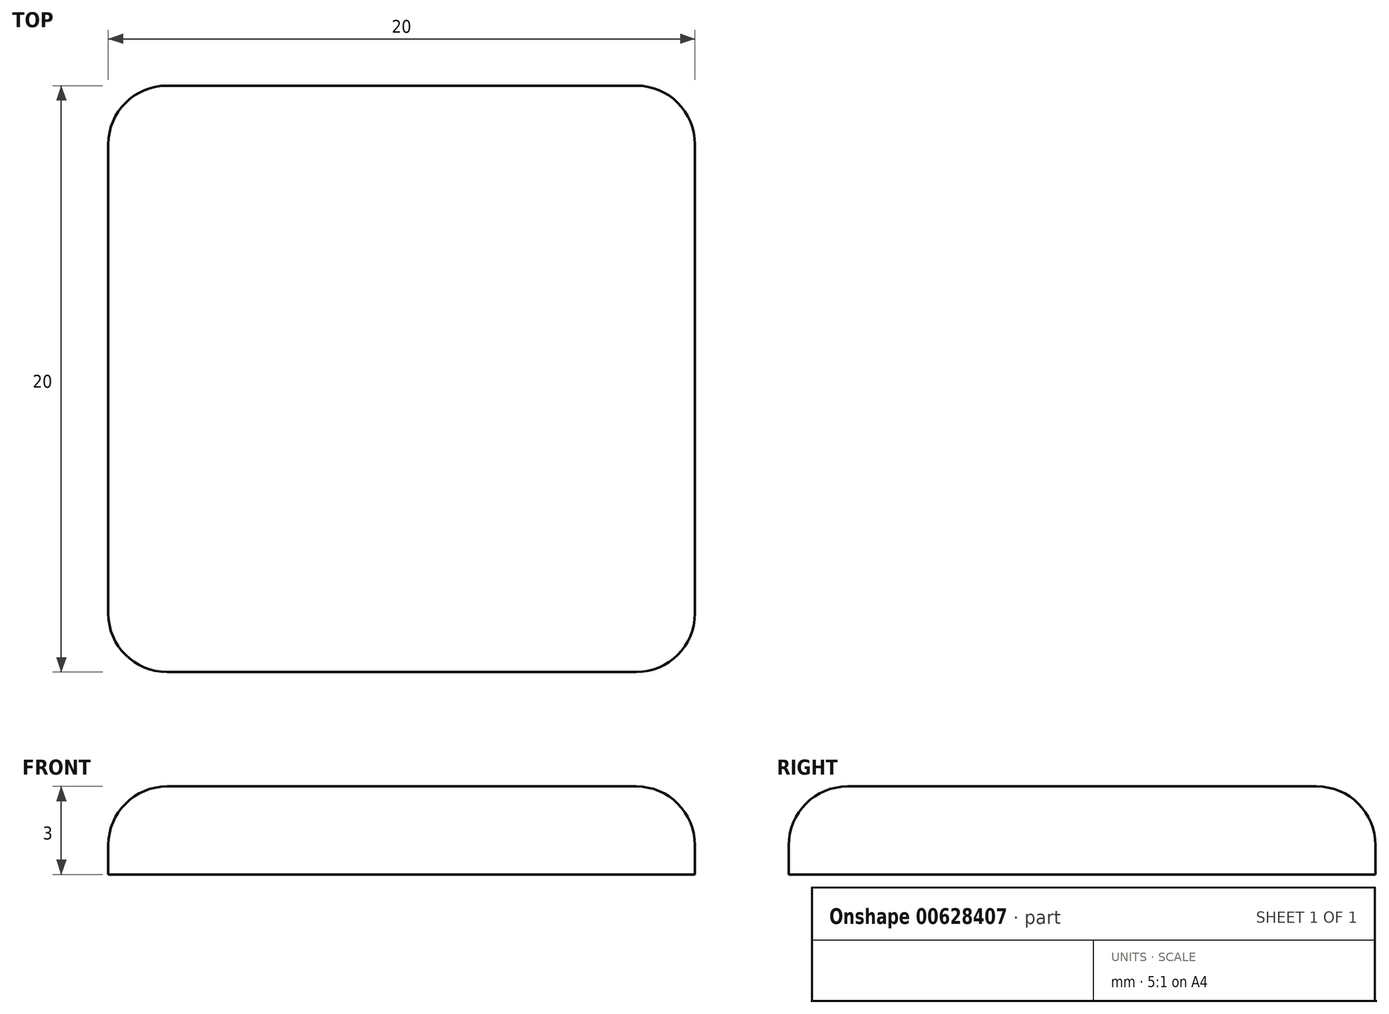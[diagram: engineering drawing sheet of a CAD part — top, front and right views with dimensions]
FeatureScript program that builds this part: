
annotation { "Feature Type Name" : "Feature", "Feature Type Description" : "" }
export const myFeature = defineFeature(function(context is Context, id is Id, definition is map)
    precondition{}
    {
        {
            var Q0;
            Q0=qCreatedBy(makeId("Top.planeOp"),FACE);
            var sketch = newSketch(context, id + "F0", { "sketchPlane" : qUnion([Q0])});
            skLineSegment(sketch, "E0.bottom", {"start": v(8, 10) * mm, "end": v(-8, 10) * mm});
            skLineSegment(sketch, "E0.top", {"start": v(8, -10) * mm, "end": v(-8, -10) * mm});
            skLineSegment(sketch, "E0.left", {"start": v(10, 8) * mm, "end": v(10, -8) * mm});
            skLineSegment(sketch, "E0.right", {"start": v(-10, 8) * mm, "end": v(-10, -8) * mm});
            skPoint(sketch, "E0.middle", {"position": v(0, 0) * mm});
            skPoint(sketch, "E1.visualSharp", {"position": v(-10, 10) * mm});
            skArc(sketch, "E1.filletArc", {"start": v(-8, 10) * mm, "mid": v(-9.41, 9.41) * mm, "end": v(-10, 8) * mm});
            skPoint(sketch, "E2.visualSharp", {"position": v(10, 10) * mm});
            skArc(sketch, "E2.filletArc", {"start": v(10, 8) * mm, "mid": v(9.41, 9.41) * mm, "end": v(8, 10) * mm});
            skPoint(sketch, "E3.visualSharp", {"position": v(10, -10) * mm});
            skArc(sketch, "E3.filletArc", {"start": v(8, -10) * mm, "mid": v(9.41, -9.41) * mm, "end": v(10, -8) * mm});
            skPoint(sketch, "E4.visualSharp", {"position": v(-10, -10) * mm});
            skArc(sketch, "E4.filletArc", {"start": v(-10, -8) * mm, "mid": v(-9.41, -9.41) * mm, "end": v(-8, -10) * mm});
            skSolve(sketch);
        }
        {
            var Q0;
            Q0=makeQuery(id+"F0.imprint","IMPRINT",FACE,{"disambiguationData":[TD([[makeQuery(id+"F0.imprint","IMPRINT",EDGE,{"derivedFrom":sQuery(id+"F0.wireOp",EDGE,"E0.bottom")}),1.0]])]});
            extrude(context, id + "F1", {"entities" : qUnion([Q0]), "depth" : 3 * mm, "offsetDistance" : 25 * mm});
        }
        {
            var Q0;
            Q0=makeQuery(id+"F1.opExtrude","CAP_EDGE",EDGE,{"disambiguationData":[OSD([sQuery(id+"F0.wireOp",EDGE,"E1.filletArc")])],"isStart":false});
            fillet(context, id + "F2", {"entities" : qUnion([Q0]), "radius" : 2 * mm, "tangentPropagation" : true, "allowEdgeOverflow" : false});
        }
    });
